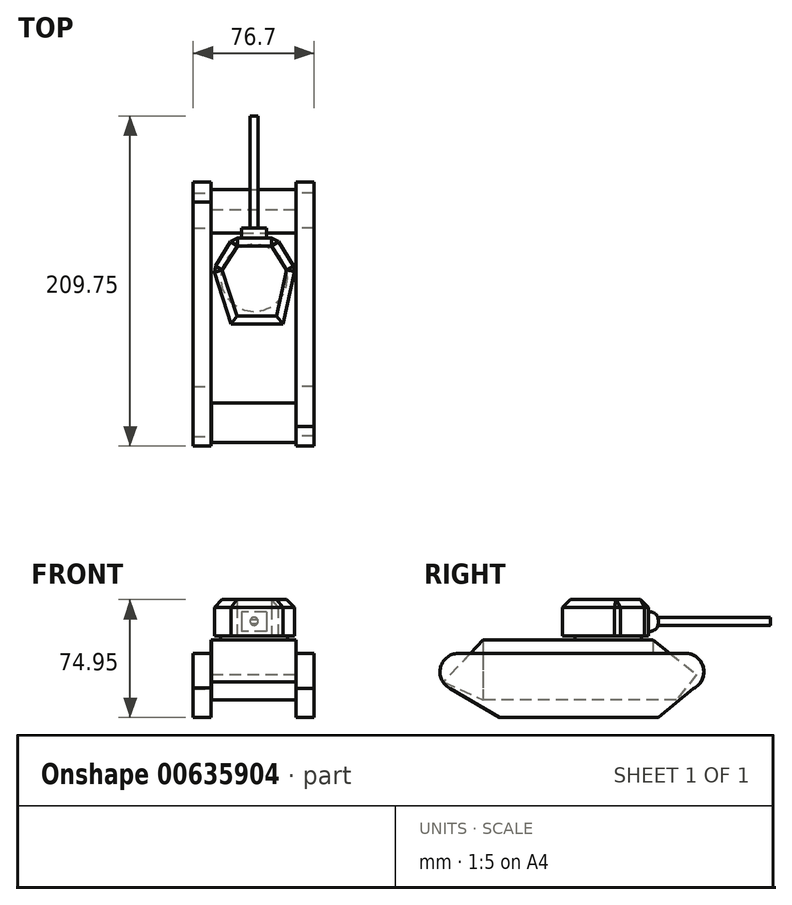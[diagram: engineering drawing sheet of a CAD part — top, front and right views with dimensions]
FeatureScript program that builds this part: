
annotation { "Feature Type Name" : "Feature", "Feature Type Description" : "" }
export const myFeature = defineFeature(function(context is Context, id is Id, definition is map)
    precondition{}
    {
        {
            var Q0;
            Q0=qCreatedBy(makeId("Top.planeOp"),FACE);
            var sketch = newSketch(context, id + "F0", { "sketchPlane" : qUnion([Q0])});
            skLineSegment(sketch, "E0.bottom", {"start": v(-27.22, 57.6) * mm, "end": v(26.62, 57.6) * mm});
            skLineSegment(sketch, "E0.top", {"start": v(-27.22, -50.38) * mm, "end": v(26.62, -50.38) * mm});
            skLineSegment(sketch, "E0.left", {"start": v(-27.22, 57.6) * mm, "end": v(-27.22, -50.38) * mm});
            skLineSegment(sketch, "E0.right", {"start": v(26.62, 57.6) * mm, "end": v(26.62, -50.38) * mm});
            skSolve(sketch);
        }
        {
            var Q0;
            Q0 = qSketchRegion(id + "F0", true);
            extrude(context, id + "F1", {"entities" : qUnion([Q0]), "depth" : 38.1 * mm, "offsetDistance" : 25.4 * mm});
        }
        {
            var Q0;
            Q0=makeQuery(id+"F1.opExtrude","SWEPT_FACE",FACE,{"disambiguationData":[OSD([sQuery(id+"F0.wireOp",EDGE,"E0.right")])]});
            var sketch = newSketch(context, id + "F2", { "sketchPlane" : qUnion([Q0])});
            skLineSegment(sketch, "E1", {"start": v(-50.38, 38.1) * mm, "end": v(-75.35, 11.58) * mm});
            skLineSegment(sketch, "E2", {"start": v(-75.35, 11.58) * mm, "end": v(-50.38, 0) * mm});
            skLineSegment(sketch, "E3", {"start": v(-50.38, 0) * mm, "end": v(-50.38, 38.1) * mm});
            skSolve(sketch);
        }
        {
            var Q0;
            Q0 = qSketchRegion(id + "F2", true);
            extrude(context, id + "F3", {"entities" : qUnion([Q0]), "operationType" : NewBodyOperationType.ADD, "oppositeDirection" : true, "depth" : 53.77 * mm, "offsetDistance" : 25.4 * mm});
        }
        {
            var Q0;
            Q0=makeQuery(id+"F3.boolean.opBoolean","MERGE",FACE,{"derivedFrom":[makeQuery(id+"F1.opExtrude","SWEPT_FACE",FACE,{"disambiguationData":[OSD([sQuery(id+"F0.wireOp",EDGE,"E0.right")])]}),makeQuery(id+"F3.opExtrude","CAP_FACE",FACE,{"disambiguationData":[OSD([sQuery(id+"F2.wireOp",EDGE,"E1"),sQuery(id+"F2.wireOp",EDGE,"E2"),sQuery(id+"F2.wireOp",EDGE,"E3")])],"isStart":true})]});
            var sketch = newSketch(context, id + "F4", { "sketchPlane" : qUnion([Q0])});
            skLineSegment(sketch, "E4", {"start": v(57.6, 38.1) * mm, "end": v(85.3, 16.23) * mm});
            skLineSegment(sketch, "E5", {"start": v(85.3, 16.23) * mm, "end": v(72.49, 0) * mm});
            skLineSegment(sketch, "E6", {"start": v(72.49, 0) * mm, "end": v(57.6, 0) * mm});
            skSolve(sketch);
        }
        {
            var Q0;
            Q0 = qSketchRegion(id + "F4", true);
            var Q1;
            Q1=makeQuery(id+"F4.imprint","IMPRINT",FACE,{"disambiguationData":[TD([[makeQuery(id+"F4.imprint","IMPRINT",EDGE,{"derivedFrom":sQuery(id+"F4.wireOp",EDGE,"E4")}),-1.0]])]});
            extrude(context, id + "F5", {"entities" : qUnion([Q0, Q1]), "operationType" : NewBodyOperationType.ADD, "oppositeDirection" : true, "depth" : 53.87 * mm, "offsetDistance" : 25.4 * mm});
        }
        {
            var Q0;
            {var subQ0=sQuery(id+"F0.wireOp",EDGE,"E0.right");Q0=makeQuery(id+"F5.boolean.opBoolean","MERGE",FACE,{"derivedFrom":[makeQuery(id+"F3.boolean.opBoolean","MERGE",FACE,{"derivedFrom":[makeQuery(id+"F1.opExtrude","SWEPT_FACE",FACE,{"disambiguationData":[OSD([subQ0])]}),makeQuery(id+"F3.opExtrude","CAP_FACE",FACE,{"disambiguationData":[OSD([sQuery(id+"F2.wireOp",EDGE,"E1"),sQuery(id+"F2.wireOp",EDGE,"E2"),sQuery(id+"F2.wireOp",EDGE,"E3")])],"isStart":true})]}),makeQuery(id+"F5.opExtrude","CAP_FACE",FACE,{"disambiguationData":[OSD([sQuery(id+"F0.wireOp",EDGE,"E0.bottom"),subQ0,sQuery(id+"F4.wireOp",EDGE,"E4"),sQuery(id+"F4.wireOp",EDGE,"E5"),sQuery(id+"F4.wireOp",EDGE,"E6")])],"isStart":true})]});}
            var sketch = newSketch(context, id + "F6", { "sketchPlane" : qUnion([Q0])});
            skCircle(sketch, "E7", {"center": v(-65.9, 17.83) * mm, "radius": 11.8 * mm});
            skPoint(sketch, "E8.center.orphan", {"position": v(78.1, 17.83) * mm});
            skCircle(sketch, "E9", {"center": v(78.1, 17.83) * mm, "radius": 11.8 * mm});
            skLineSegment(sketch, "E10", {"start": v(-66.67, 29.6) * mm, "end": v(78.1, 29.63) * mm});
            skLineSegment(sketch, "E11", {"start": v(-71.38, 7.38) * mm, "end": v(-39.88, -11.19) * mm});
            skLineSegment(sketch, "E12", {"start": v(-39.88, -11.19) * mm, "end": v(60.98, -11.19) * mm});
            skLineSegment(sketch, "E13", {"start": v(60.98, -11.19) * mm, "end": v(83.2, 7.2) * mm});
            skSolve(sketch);
        }
        {
            var Q0;
            Q0 = qSketchRegion(id + "F6", true);
            extrude(context, id + "F7", {"entities" : qUnion([Q0]), "operationType" : NewBodyOperationType.ADD, "depth" : 11.43 * mm, "offsetDistance" : 25.4 * mm});
        }
        {
            var Q0;
            Q0=makeQuery(id+"F1.opExtrude","SWEPT_FACE",FACE,{"disambiguationData":[OSD([sQuery(id+"F0.wireOp",EDGE,"E0.left")])]});
            var sketch = newSketch(context, id + "F8", { "sketchPlane" : qUnion([Q0])});
            skCircle(sketch, "E14", {"center": v(-78.13, 17.89) * mm, "radius": 11.8 * mm});
            skCircle(sketch, "E15", {"center": v(65.87, 17.85) * mm, "radius": 11.76 * mm});
            skLineSegment(sketch, "E16", {"start": v(-77.39, 29.67) * mm, "end": v(65.87, 29.62) * mm});
            skLineSegment(sketch, "E17", {"start": v(71.61, 7.58) * mm, "end": v(39.93, -11.2) * mm});
            skLineSegment(sketch, "E18", {"start": v(39.93, -11.2) * mm, "end": v(-60.94, -11.16) * mm});
            skLineSegment(sketch, "E19", {"start": v(-60.94, -11.16) * mm, "end": v(-82.98, 7.12) * mm});
            skSolve(sketch);
        }
        {
            var Q0;
            Q0 = qSketchRegion(id + "F8", true);
            extrude(context, id + "F9", {"entities" : qUnion([Q0]), "operationType" : NewBodyOperationType.ADD, "depth" : 11.43 * mm, "offsetDistance" : 25.4 * mm});
        }
        {
            var Q0;
            Q0=makeQuery(id+"F1.opExtrude","CAP_FACE",FACE,{"disambiguationData":[OSD([sQuery(id+"F0.wireOp",EDGE,"E0.bottom"),sQuery(id+"F0.wireOp",EDGE,"E0.top"),sQuery(id+"F0.wireOp",EDGE,"E0.left"),sQuery(id+"F0.wireOp",EDGE,"E0.right")])],"isStart":false});
            var sketch = newSketch(context, id + "F10", { "sketchPlane" : qUnion([Q0])});
            skCircle(sketch, "E20", {"center": v(0, 29.12) * mm, "radius": 21.2 * mm});
            skSolve(sketch);
        }
        {
            var Q0;
            Q0 = qSketchRegion(id + "F10", true);
            extrude(context, id + "F11", {"entities" : qUnion([Q0]), "operationType" : NewBodyOperationType.ADD, "depth" : 2.54 * mm, "offsetDistance" : 25.4 * mm});
        }
        {
            var Q0;
            Q0=makeQuery(id+"F11.opExtrude","CAP_FACE",FACE,{"disambiguationData":[OSD([sQuery(id+"F10.wireOp",EDGE,"E20")])],"isStart":false});
            var sketch = newSketch(context, id + "F12", { "sketchPlane" : qUnion([Q0])});
            skLineSegment(sketch, "E21", {"start": v(-13.4, 54.6) * mm, "end": v(14.06, 54.6) * mm});
            skLineSegment(sketch, "E22", {"start": v(14.06, 54.6) * mm, "end": v(25.97, 35.07) * mm});
            skLineSegment(sketch, "E23", {"start": v(25.97, 35.07) * mm, "end": v(18.36, 0) * mm});
            skLineSegment(sketch, "E24", {"start": v(18.36, 0) * mm, "end": v(-14.68, 0) * mm});
            skLineSegment(sketch, "E25", {"start": v(-14.68, 0) * mm, "end": v(-25.81, 34.76) * mm});
            skLineSegment(sketch, "E26", {"start": v(-25.81, 34.76) * mm, "end": v(-13.4, 54.6) * mm});
            skSolve(sketch);
        }
        {
            var Q0;
            Q0 = qSketchRegion(id + "F12", true);
            extrude(context, id + "F13", {"entities" : qUnion([Q0]), "operationType" : NewBodyOperationType.ADD, "depth" : 16.76 * mm, "offsetDistance" : 25.4 * mm});
        }
        {
            var Q0;
            Q0=makeQuery(id+"F13.opExtrude","CAP_FACE",FACE,{"disambiguationData":[OSD([sQuery(id+"F12.wireOp",EDGE,"E21"),sQuery(id+"F12.wireOp",EDGE,"E22"),sQuery(id+"F12.wireOp",EDGE,"E23"),sQuery(id+"F12.wireOp",EDGE,"E24"),sQuery(id+"F12.wireOp",EDGE,"E25"),sQuery(id+"F12.wireOp",EDGE,"E26")])],"isStart":false});
            extrude(context, id + "F14", {"entities" : qUnion([Q0]), "operationType" : NewBodyOperationType.ADD, "depth" : 6.35 * mm, "offsetDistance" : 25.4 * mm});
        }
        {
            var Q0;
            Q0=makeQuery(id+"F14.opExtrude","CAP_EDGE",EDGE,{"disambiguationData":[OSD([sQuery(id+"F12.wireOp",EDGE,"E21")])],"isStart":false});
            var Q1;
            Q1=makeQuery(id+"F14.opExtrude","CAP_EDGE",EDGE,{"disambiguationData":[OSD([sQuery(id+"F12.wireOp",EDGE,"E26")])],"isStart":false});
            var Q2;
            Q2=makeQuery(id+"F14.opExtrude","CAP_EDGE",EDGE,{"disambiguationData":[OSD([sQuery(id+"F12.wireOp",EDGE,"E25")])],"isStart":false});
            var Q3;
            Q3=makeQuery(id+"F14.opExtrude","CAP_EDGE",EDGE,{"disambiguationData":[OSD([sQuery(id+"F12.wireOp",EDGE,"E24")])],"isStart":false});
            var Q4;
            Q4=makeQuery(id+"F14.opExtrude","CAP_EDGE",EDGE,{"disambiguationData":[OSD([sQuery(id+"F12.wireOp",EDGE,"E23")])],"isStart":false});
            var Q5;
            Q5=makeQuery(id+"F14.opExtrude","CAP_EDGE",EDGE,{"disambiguationData":[OSD([sQuery(id+"F12.wireOp",EDGE,"E22")])],"isStart":false});
            var Q6;
            {var subQ0=sQuery(id+"F12.wireOp",EDGE,"E26");var subQ1=sQuery(id+"F12.wireOp",EDGE,"E21");Q6=makeQuery(id+"F14.boolean.opBoolean","MERGE",EDGE,{"derivedFrom":[makeQuery(id+"F13.opExtrude","SWEPT_EDGE",EDGE,{"disambiguationData":[OSD([subQ1,subQ0])]}),makeQuery(id+"F14.opExtrude","SWEPT_EDGE",EDGE,{"disambiguationData":[OSD([subQ1,subQ0])]})]});}
            var Q7;
            {var subQ0=sQuery(id+"F12.wireOp",EDGE,"E26");var subQ1=sQuery(id+"F12.wireOp",EDGE,"E25");Q7=makeQuery(id+"F14.boolean.opBoolean","MERGE",EDGE,{"derivedFrom":[makeQuery(id+"F13.opExtrude","SWEPT_EDGE",EDGE,{"disambiguationData":[OSD([subQ1,subQ0])]}),makeQuery(id+"F14.opExtrude","SWEPT_EDGE",EDGE,{"disambiguationData":[OSD([subQ1,subQ0])]})]});}
            var Q8;
            {var subQ0=sQuery(id+"F12.wireOp",EDGE,"E22");var subQ1=sQuery(id+"F12.wireOp",EDGE,"E21");Q8=makeQuery(id+"F14.boolean.opBoolean","MERGE",EDGE,{"derivedFrom":[makeQuery(id+"F13.opExtrude","SWEPT_EDGE",EDGE,{"disambiguationData":[OSD([subQ1,subQ0])]}),makeQuery(id+"F14.opExtrude","SWEPT_EDGE",EDGE,{"disambiguationData":[OSD([subQ1,subQ0])]})]});}
            var Q9;
            {var subQ0=sQuery(id+"F12.wireOp",EDGE,"E23");var subQ1=sQuery(id+"F12.wireOp",EDGE,"E22");Q9=makeQuery(id+"F14.boolean.opBoolean","MERGE",EDGE,{"derivedFrom":[makeQuery(id+"F13.opExtrude","SWEPT_EDGE",EDGE,{"disambiguationData":[OSD([subQ1,subQ0])]}),makeQuery(id+"F14.opExtrude","SWEPT_EDGE",EDGE,{"disambiguationData":[OSD([subQ1,subQ0])]})]});}
            chamfer(context, id + "F15", {"entities" : qUnion([Q0, Q1, Q2, Q3, Q4, Q5, Q6, Q7, Q8, Q9]), "width" : 5.08 * mm, "tangentPropagation" : true});
        }
        {
            var Q0;
            {var subQ0=sQuery(id+"F12.wireOp",EDGE,"E21");Q0=makeQuery(id+"F14.boolean.opBoolean","MERGE",FACE,{"derivedFrom":[makeQuery(id+"F13.opExtrude","SWEPT_FACE",FACE,{"disambiguationData":[OSD([subQ0])]}),makeQuery(id+"F14.opExtrude","SWEPT_FACE",FACE,{"disambiguationData":[OSD([subQ0])]})]});}
            var sketch = newSketch(context, id + "F16", { "sketchPlane" : qUnion([Q0])});
            skLineSegment(sketch, "E27.bottom", {"start": v(-7.87, 55.98) * mm, "end": v(7.87, 55.98) * mm});
            skLineSegment(sketch, "E27.top", {"start": v(-7.87, 43.64) * mm, "end": v(7.87, 43.64) * mm});
            skLineSegment(sketch, "E27.left", {"start": v(-7.87, 55.98) * mm, "end": v(-7.87, 43.64) * mm});
            skLineSegment(sketch, "E27.right", {"start": v(7.87, 55.98) * mm, "end": v(7.87, 43.64) * mm});
            skSolve(sketch);
        }
        {
            var Q0;
            Q0 = qSketchRegion(id + "F16", true);
            extrude(context, id + "F17", {"entities" : qUnion([Q0]), "operationType" : NewBodyOperationType.ADD, "depth" : 6.35 * mm, "offsetDistance" : 25.4 * mm});
        }
        {
            var Q0;
            Q0=makeQuery(id+"F17.opExtrude","CAP_EDGE",EDGE,{"disambiguationData":[OSD([sQuery(id+"F16.wireOp",EDGE,"E27.bottom")])],"isStart":false});
            var Q1;
            Q1=makeQuery(id+"F17.opExtrude","CAP_EDGE",EDGE,{"disambiguationData":[OSD([sQuery(id+"F16.wireOp",EDGE,"E27.top")])],"isStart":false});
            fillet(context, id + "F18", {"entities" : qUnion([Q0, Q1]), "radius" : 5.08 * mm, "tangentPropagation" : true, "allowEdgeOverflow" : false});
        }
        {
            var Q0;
            Q0=makeQuery(id+"F17.opExtrude","CAP_FACE",FACE,{"disambiguationData":[OSD([sQuery(id+"F16.wireOp",EDGE,"E27.bottom"),sQuery(id+"F16.wireOp",EDGE,"E27.top"),sQuery(id+"F16.wireOp",EDGE,"E27.left"),sQuery(id+"F16.wireOp",EDGE,"E27.right")])],"isStart":false});
            var sketch = newSketch(context, id + "F19", { "sketchPlane" : qUnion([Q0])});
            skCircle(sketch, "E28", {"center": v(0, 50) * mm, "radius": 2.51 * mm});
            skPoint(sketch, "E28.centerSnap0", {"position": v(0, 48.72) * mm});
            skSolve(sketch);
        }
        {
            var Q0;
            Q0 = qSketchRegion(id + "F19", true);
            extrude(context, id + "F20", {"entities" : qUnion([Q0]), "operationType" : NewBodyOperationType.ADD, "depth" : 71.12 * mm, "offsetDistance" : 25.4 * mm});
        }
    });
